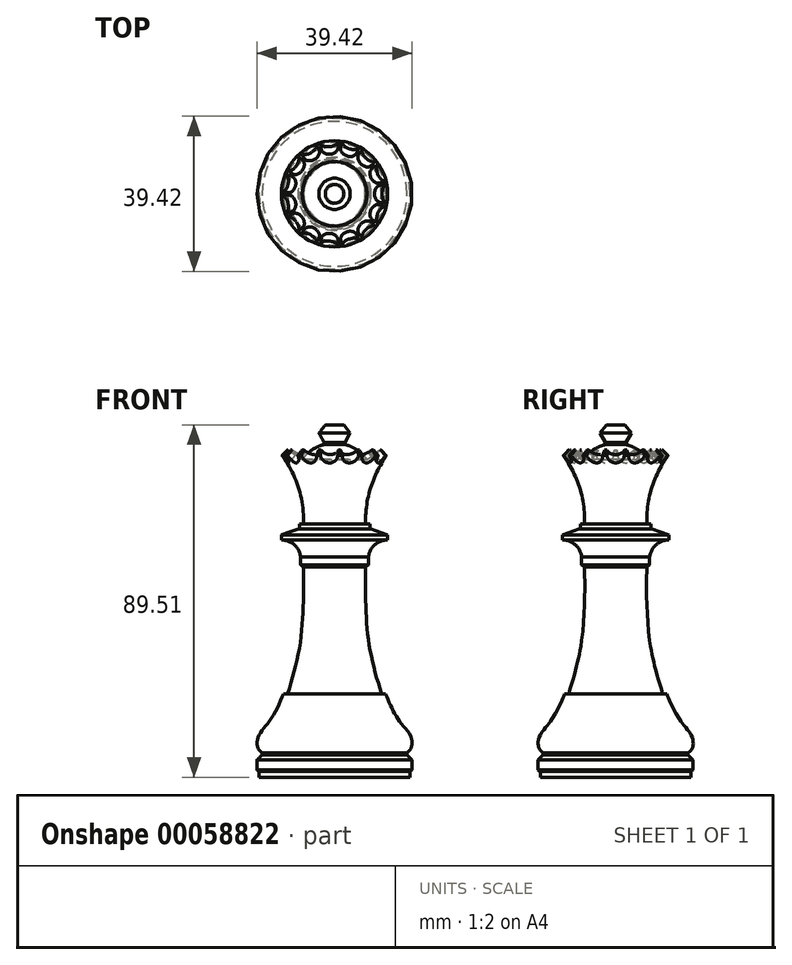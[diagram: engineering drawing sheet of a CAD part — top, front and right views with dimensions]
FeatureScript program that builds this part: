
annotation { "Feature Type Name" : "Feature", "Feature Type Description" : "" }
export const myFeature = defineFeature(function(context is Context, id is Id, definition is map)
    precondition{}
    {
        {
            var Q0;
            Q0=qCreatedBy(makeId("Front.planeOp"),FACE);
            var sketch = newSketch(context, id + "F0", { "sketchPlane" : qUnion([Q0])});
            skLineSegment(sketch, "E0", {"start": v(0, 58.88) * mm, "end": v(0, -49.54) * mm, "construction": true});
            skLineSegment(sketch, "E1", {"start": v(0, 51.46) * mm, "end": v(2.35, 51.46) * mm});
            skLineSegment(sketch, "E2", {"start": v(2.35, 51.46) * mm, "end": v(3.97, 49.38) * mm});
            skLineSegment(sketch, "E3", {"start": v(3.97, 49.38) * mm, "end": v(2.64, 47.02) * mm});
            skLineSegment(sketch, "E4", {"start": v(2.64, 47.02) * mm, "end": v(2.64, 46.47) * mm});
            skArc(sketch, "E5", {"start": v(8.2, 42.67) * mm, "mid": v(5.77, 45.08) * mm, "end": v(2.64, 46.47) * mm});
            skLineSegment(sketch, "E6", {"start": v(8.2, 42.67) * mm, "end": v(11.98, 45.15) * mm});
            skLineSegment(sketch, "E7", {"start": v(11.98, 45.15) * mm, "end": v(13.34, 43.68) * mm});
            skArc(sketch, "E8", {"start": v(13.34, 43.68) * mm, "mid": v(9.15, 35.46) * mm, "end": v(7.9, 26.31) * mm});
            skLineSegment(sketch, "E9", {"start": v(7.9, 26.31) * mm, "end": v(8.95, 26.31) * mm});
            skLineSegment(sketch, "E10", {"start": v(8.95, 26.31) * mm, "end": v(8.95, 24.97) * mm});
            skLineSegment(sketch, "E11", {"start": v(8.95, 24.97) * mm, "end": v(9.28, 24.97) * mm});
            skLineSegment(sketch, "E12", {"start": v(9.28, 24.97) * mm, "end": v(13.5, 23.51) * mm});
            skLineSegment(sketch, "E13", {"start": v(13.5, 23.51) * mm, "end": v(13.5, 22.25) * mm});
            skArc(sketch, "E14", {"start": v(13.5, 22.25) * mm, "mid": v(10.22, 21) * mm, "end": v(8.63, 17.88) * mm});
            skLineSegment(sketch, "E15", {"start": v(8.63, 17.88) * mm, "end": v(8.63, 15.88) * mm});
            skLineSegment(sketch, "E16", {"start": v(8.63, 15.88) * mm, "end": v(7.9, 15.34) * mm});
            skFitSpline(sketch, "E17", {"points": [v(7.9, 15.34) * mm, v(7.9, 6.9) * mm, v(8.92, -5.17) * mm, v(11.92, -16.85) * mm], "startDerivative": vector(-0.36, -27.2) * mm, "endDerivative": vector(9.81, -32.47) * mm});
            skLineSegment(sketch, "E18", {"start": v(11.92, -16.85) * mm, "end": v(12.98, -16.85) * mm});
            skFitSpline(sketch, "E19", {"points": [v(12.98, -16.85) * mm, v(16.44, -23.7) * mm, v(19.2, -27.34) * mm, v(19.63, -30.14) * mm, v(18.4, -31.86) * mm], "startDerivative": vector(7.11, -18.88) * mm, "endDerivative": vector(-10.54, -7.89) * mm});
            skLineSegment(sketch, "E20", {"start": v(18.4, -31.86) * mm, "end": v(18.4, -32.33) * mm});
            skLineSegment(sketch, "E21", {"start": v(18.4, -32.33) * mm, "end": v(19.7, -33.62) * mm});
            skLineSegment(sketch, "E22", {"start": v(19.7, -33.62) * mm, "end": v(19.7, -36.24) * mm});
            skLineSegment(sketch, "E23", {"start": v(19.7, -36.24) * mm, "end": v(19.15, -36.59) * mm});
            skLineSegment(sketch, "E24", {"start": v(19.15, -36.59) * mm, "end": v(19.15, -38.05) * mm});
            skLineSegment(sketch, "E25", {"start": v(19.15, -38.05) * mm, "end": v(0, -38.05) * mm});
            skLineSegment(sketch, "E26", {"start": v(0, -38.05) * mm, "end": v(0, 51.46) * mm});
            skSolve(sketch);
        }
        {
            var Q0;
            Q0=makeQuery(id+"F0.imprint","IMPRINT",FACE,{"disambiguationData":[TD([[makeQuery(id+"F0.imprint","IMPRINT",EDGE,{"derivedFrom":sQuery(id+"F0.wireOp",EDGE,"E1")}),-1.0]])]});
            var Q1;
            Q1=sQuery(id+"F0.wireOp",EDGE,"E26");
            revolve(context, id + "F1", {"entities" : qUnion([Q0]), "axis" : qUnion([Q1]), "revolveType" : RevolveType.FULL});
        }
        {
            var Q0;
            Q0=qCreatedBy(makeId("Front.planeOp"),FACE);
            var sketch = newSketch(context, id + "F2", { "sketchPlane" : qUnion([Q0])});
            skLineSegment(sketch, "E27", {"start": v(11.98, 45.15) * mm, "end": v(13.34, 43.68) * mm});
            skLineSegment(sketch, "E28", {"start": v(11.98, 45.15) * mm, "end": v(11.25, 45.94) * mm});
            skLineSegment(sketch, "E29", {"start": v(13.34, 43.68) * mm, "end": v(14.35, 42.6) * mm});
            skLineSegment(sketch, "E30", {"start": v(11.25, 45.94) * mm, "end": v(12.87, 47.44) * mm});
            skLineSegment(sketch, "E31", {"start": v(12.87, 47.44) * mm, "end": v(15.96, 44.1) * mm});
            skLineSegment(sketch, "E32", {"start": v(14.35, 42.6) * mm, "end": v(15.96, 44.1) * mm});
            skSolve(sketch);
        }
        {
            var Q0;
            Q0=makeQuery(id+"F2.imprint","IMPRINT",FACE,{"disambiguationData":[TD([[makeQuery(id+"F2.imprint","IMPRINT",EDGE,{"derivedFrom":sQuery(id+"F2.wireOp",EDGE,"E27")}),1.0]])]});
            var Q1;
            Q1=sQuery(id+"F2.wireOp",EDGE,"E27");
            revolve(context, id + "F3", {"entities" : qUnion([Q0]), "axis" : qUnion([Q1]), "revolveType" : RevolveType.FULL});
        }
        {
            var Q0;
            Q0=makeQuery(id+"F3.opRevolve","SWEPT_BODY",BODY,{"disambiguationData":[OSD([sQuery(id+"F2.wireOp",EDGE,"E27"),sQuery(id+"F2.wireOp",EDGE,"E28"),sQuery(id+"F2.wireOp",EDGE,"E29"),sQuery(id+"F2.wireOp",EDGE,"E30"),sQuery(id+"F2.wireOp",EDGE,"E31"),sQuery(id+"F2.wireOp",EDGE,"E32")])]});
            var Q1;
            Q1=sQuery(id+"F0.wireOp",EDGE,"E26");
            circularPattern(context, id + "F4", {"operationType" : NewBodyOperationType.REMOVE, "entities" : qUnion([Q0]), "axis" : qUnion([Q1]), "angle" : 360 * degree, "instanceCount" : 15, "oppositeDirection" : true, "equalSpace" : true});
        }
    });
